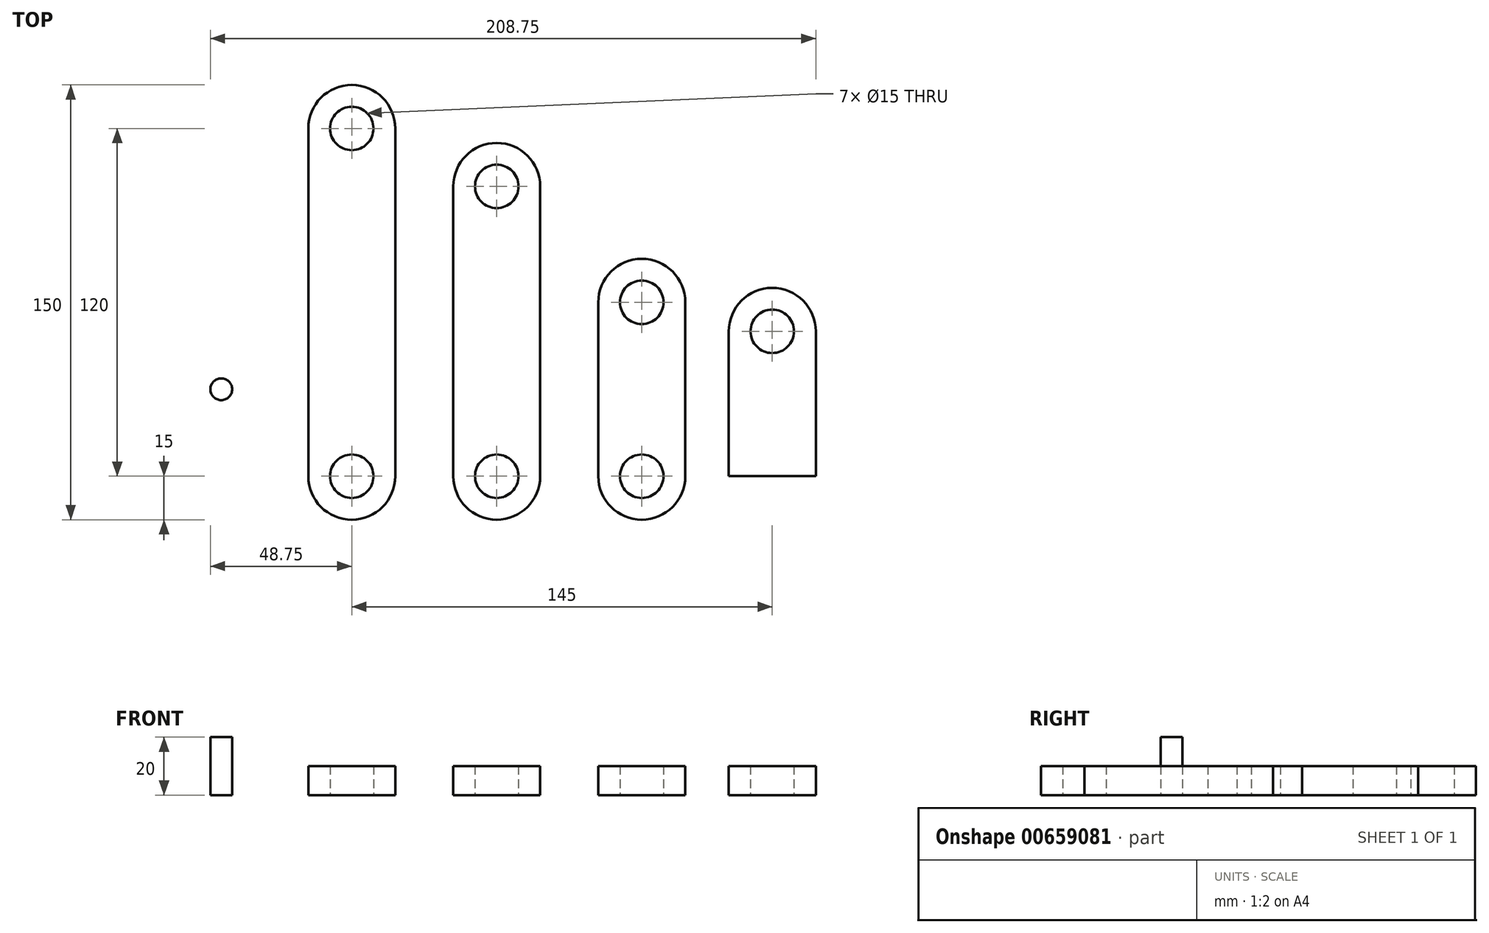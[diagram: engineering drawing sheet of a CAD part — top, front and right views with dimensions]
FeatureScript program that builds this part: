
annotation { "Feature Type Name" : "Feature", "Feature Type Description" : "" }
export const myFeature = defineFeature(function(context is Context, id is Id, definition is map)
    precondition{}
    {
        {
            assignVariable(context, id + "F0", {"name" : "thickness", "anyValue" : 10});
        }
        {
            var Q0;
            Q0=qCreatedBy(makeId("Top.planeOp"),FACE);
            var sketch = newSketch(context, id + "F1", { "sketchPlane" : qUnion([Q0])});
            skCircle(sketch, "E0", {"center": v(-50, 120) * mm, "radius": 7.5 * mm});
            skArc(sketch, "E1", {"start": v(-35, 120) * mm, "mid": v(-50, 135) * mm, "end": v(-65, 120) * mm});
            skLineSegment(sketch, "E2", {"start": v(-65, 120) * mm, "end": v(-65, 0) * mm});
            skLineSegment(sketch, "E3", {"start": v(-35, 120) * mm, "end": v(-35, 0) * mm});
            skLineSegment(sketch, "E4", {"start": v(-71.7, 60) * mm, "end": v(-14.35, 60) * mm, "construction": true});
            skCircle(sketch, "E5.MirrorC", {"center": v(-50, 0) * mm, "radius": 7.5 * mm});
            skArc(sketch, "E6.MirrorCS", {"start": v(-35, 0) * mm, "mid": v(-50, -15) * mm, "end": v(-65, 0) * mm});
            skArc(sketch, "E7", {"start": v(-15, 0) * mm, "mid": v(0, -15) * mm, "end": v(15, 0) * mm});
            skCircle(sketch, "E8", {"center": v(0, 0) * mm, "radius": 7.5 * mm});
            skLineSegment(sketch, "E9", {"start": v(-15, 0) * mm, "end": v(-15, 50) * mm});
            skLineSegment(sketch, "E10", {"start": v(-24, 50) * mm, "end": v(25.2, 50) * mm, "construction": true});
            skLineSegment(sketch, "E11", {"start": v(15, 0) * mm, "end": v(15, 50) * mm});
            skLineSegment(sketch, "E12.MirrorCS", {"start": v(15, 100) * mm, "end": v(15, 50) * mm});
            skLineSegment(sketch, "E13.MirrorCS", {"start": v(-15, 100) * mm, "end": v(-15, 50) * mm});
            skCircle(sketch, "E14.MirrorC", {"center": v(0, 100) * mm, "radius": 7.5 * mm});
            skArc(sketch, "E15.MirrorCS", {"start": v(-15, 100) * mm, "mid": v(0, 115) * mm, "end": v(15, 100) * mm});
            skCircle(sketch, "E16", {"center": v(50, 0) * mm, "radius": 7.5 * mm});
            skArc(sketch, "E17", {"start": v(35, 0) * mm, "mid": v(50, -15) * mm, "end": v(65, 0) * mm});
            skLineSegment(sketch, "E18", {"start": v(35, 0) * mm, "end": v(35, 30) * mm});
            skLineSegment(sketch, "E19", {"start": v(28.95, 30) * mm, "end": v(71.81, 30) * mm, "construction": true});
            skLineSegment(sketch, "E20", {"start": v(65, 0) * mm, "end": v(65, 30) * mm});
            skLineSegment(sketch, "E21.MirrorCS", {"start": v(35, 60) * mm, "end": v(35, 30) * mm});
            skLineSegment(sketch, "E22.MirrorCS", {"start": v(65, 60) * mm, "end": v(65, 30) * mm});
            skCircle(sketch, "E23.MirrorC", {"center": v(50, 60) * mm, "radius": 7.5 * mm});
            skArc(sketch, "E24.MirrorCS", {"start": v(35, 60) * mm, "mid": v(50, 75) * mm, "end": v(65, 60) * mm});
            skLineSegment(sketch, "E25.bottom", {"start": v(80, 0) * mm, "end": v(110, 0) * mm});
            skLineSegment(sketch, "E25.left", {"start": v(80, 0) * mm, "end": v(80, 50) * mm});
            skLineSegment(sketch, "E25.right", {"start": v(110, 0) * mm, "end": v(110, 50) * mm});
            skArc(sketch, "E26", {"start": v(110, 50) * mm, "mid": v(95, 65) * mm, "end": v(80, 50) * mm});
            skCircle(sketch, "E27", {"center": v(95, 50) * mm, "radius": 7.5 * mm});
            skCircle(sketch, "E28", {"center": v(-95, 30) * mm, "radius": 3.75 * mm});
            skSolve(sketch);
        }
        {
            var Q0;
            Q0=makeQuery(id+"F1.imprint","IMPRINT",FACE,{"disambiguationData":[TD([[makeQuery(id+"F1.imprint","IMPRINT",EDGE,{"derivedFrom":sQuery(id+"F1.wireOp",EDGE,"E0")}),-1.0]])]});
            var Q1;
            Q1=makeQuery(id+"F1.imprint","IMPRINT",FACE,{"disambiguationData":[TD([[makeQuery(id+"F1.imprint","IMPRINT",EDGE,{"derivedFrom":sQuery(id+"F1.wireOp",EDGE,"E7")}),1.0]])]});
            var Q2;
            Q2=makeQuery(id+"F1.imprint","IMPRINT",FACE,{"disambiguationData":[TD([[makeQuery(id+"F1.imprint","IMPRINT",EDGE,{"derivedFrom":sQuery(id+"F1.wireOp",EDGE,"E16")}),-1.0]])]});
            var Q3;
            Q3=makeQuery(id+"F1.imprint","IMPRINT",FACE,{"disambiguationData":[TD([[makeQuery(id+"F1.imprint","IMPRINT",EDGE,{"derivedFrom":sQuery(id+"F1.wireOp",EDGE,"E25.bottom")}),1.0]])]});
            extrude(context, id + "F2", {"entities" : qUnion([Q0, Q1, Q2, Q3]), "depth" : (getVariable(context, 'thickness')) * mm, "offsetDistance" : 25 * mm});
        }
        {
            var Q0;
            Q0=makeQuery(id+"F1.imprint","IMPRINT",FACE,{"disambiguationData":[TD([[makeQuery(id+"F1.imprint","IMPRINT",EDGE,{"derivedFrom":sQuery(id+"F1.wireOp",EDGE,"E28")}),1.0]])]});
            extrude(context, id + "F3", {"entities" : qUnion([Q0]), "depth" : (getVariable(context, 'thickness') * 2) * mm, "offsetDistance" : 25 * mm});
        }
    });
